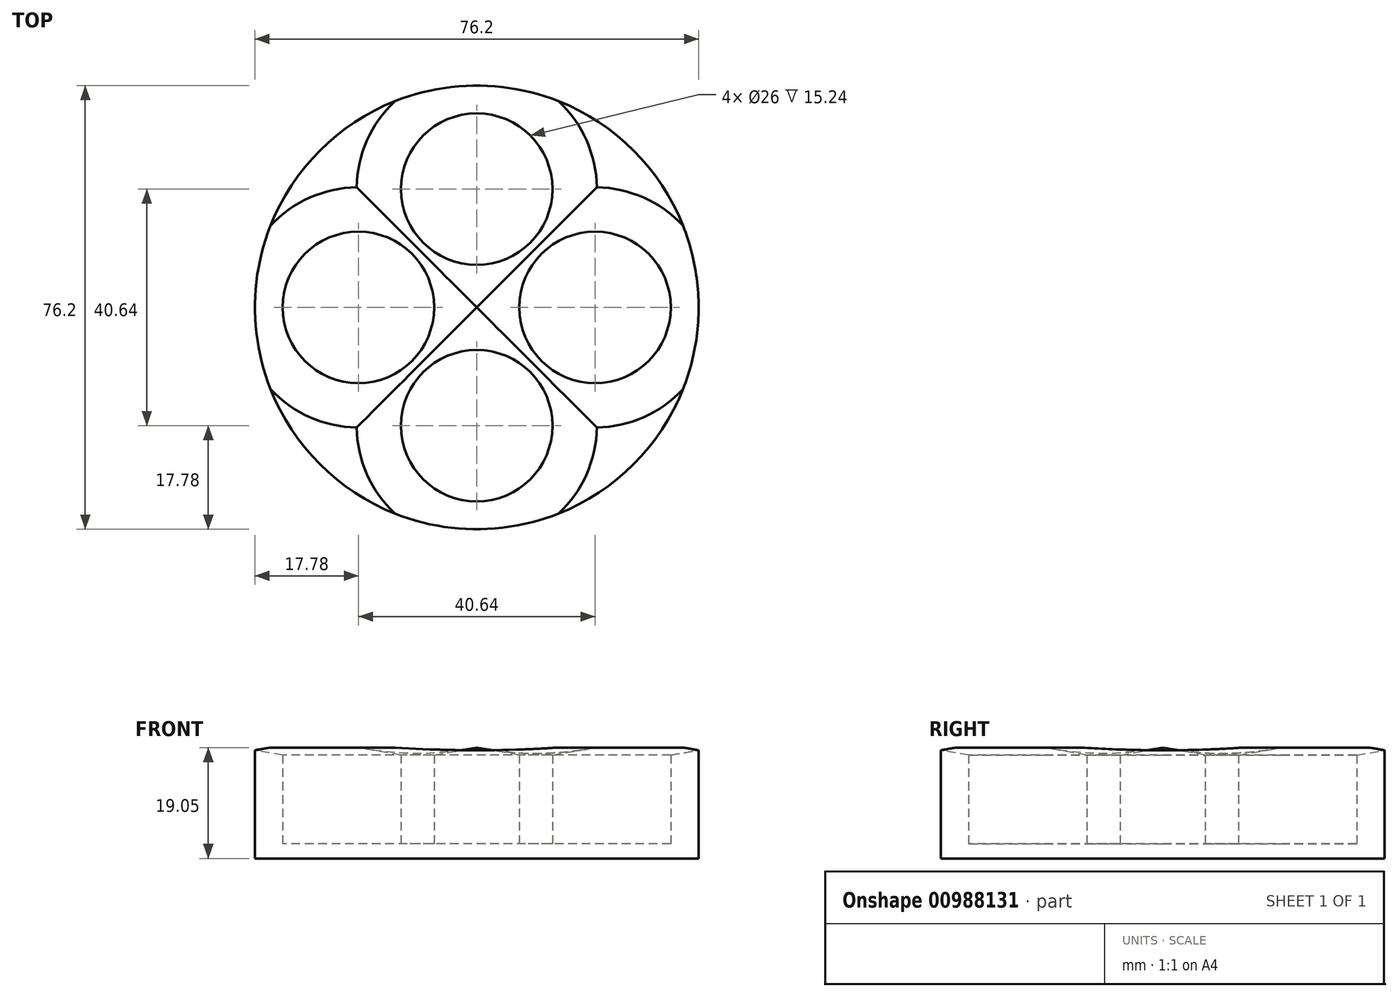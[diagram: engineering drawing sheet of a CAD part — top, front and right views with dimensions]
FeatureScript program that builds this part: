
annotation { "Feature Type Name" : "Feature", "Feature Type Description" : "" }
export const myFeature = defineFeature(function(context is Context, id is Id, definition is map)
    precondition{}
    {
        {
            var Q0;
            Q0=qCreatedBy(makeId("Top.planeOp"),FACE);
            var sketch = newSketch(context, id + "F0", { "sketchPlane" : qUnion([Q0])});
            skCircle(sketch, "E0", {"center": v(0, 0) * mm, "radius": 38.1 * mm});
            skCircle(sketch, "E1", {"center": v(0, 20.32) * mm, "radius": 13 * mm});
            skLineSegment(sketch, "E2", {"start": v(0, 20.32) * mm, "end": v(0, 0) * mm, "construction": true});
            skCircle(sketch, "E3", {"center": v(21.55, 21.55) * mm, "radius": 3.18 * mm});
            skLineSegment(sketch, "E4", {"start": v(0, 0) * mm, "end": v(21.55, 21.55) * mm, "construction": true});
            skCircle(sketch, "E5", {"center": v(21.55, 21.55) * mm, "radius": 5.55 * mm, "construction": true});
            skCircle(sketch, "E6.1.0", {"center": v(-20.32, 0) * mm, "radius": 13 * mm});
            skCircle(sketch, "E6.1.1", {"center": v(-21.55, 21.55) * mm, "radius": 3.18 * mm});
            skCircle(sketch, "E6.2.0", {"center": v(0, -20.32) * mm, "radius": 13 * mm});
            skCircle(sketch, "E6.2.1", {"center": v(-21.55, -21.55) * mm, "radius": 3.18 * mm});
            skCircle(sketch, "E6.3.0", {"center": v(20.32, 0) * mm, "radius": 13 * mm});
            skCircle(sketch, "E6.3.1", {"center": v(21.55, -21.55) * mm, "radius": 3.18 * mm});
            skSolve(sketch);
        }
        {
            var Q0;
            Q0=makeQuery(id+"F0.imprint","IMPRINT",FACE,{"disambiguationData":[TD([[makeQuery(id+"F0.imprint","IMPRINT",EDGE,{"derivedFrom":sQuery(id+"F0.wireOp",EDGE,"E0")}),1.0]])]});
            var Q1;
            Q1=makeQuery(id+"F0.imprint","IMPRINT",FACE,{"disambiguationData":[TD([[makeQuery(id+"F0.imprint","IMPRINT",EDGE,{"derivedFrom":sQuery(id+"F0.wireOp",EDGE,"E6.1.1")}),1.0]])]});
            var Q2;
            Q2=makeQuery(id+"F0.imprint","IMPRINT",FACE,{"disambiguationData":[TD([[makeQuery(id+"F0.imprint","IMPRINT",EDGE,{"derivedFrom":sQuery(id+"F0.wireOp",EDGE,"E6.2.1")}),1.0]])]});
            var Q3;
            Q3=makeQuery(id+"F0.imprint","IMPRINT",FACE,{"disambiguationData":[TD([[makeQuery(id+"F0.imprint","IMPRINT",EDGE,{"derivedFrom":sQuery(id+"F0.wireOp",EDGE,"E6.3.1")}),1.0]])]});
            var Q4;
            Q4=makeQuery(id+"F0.imprint","IMPRINT",FACE,{"disambiguationData":[TD([[makeQuery(id+"F0.imprint","IMPRINT",EDGE,{"derivedFrom":sQuery(id+"F0.wireOp",EDGE,"E3")}),1.0]])]});
            extrude(context, id + "F1", {"entities" : qUnion([Q0, Q1, Q2, Q3, Q4]), "depth" : 19.05 * mm, "offsetDistance" : 25.4 * mm});
        }
        {
            var Q0;
            Q0=makeQuery(id+"F0.imprint","IMPRINT",FACE,{"disambiguationData":[TD([[makeQuery(id+"F0.imprint","IMPRINT",EDGE,{"derivedFrom":sQuery(id+"F0.wireOp",EDGE,"E0")}),1.0]])]});
            var Q1;
            Q1=makeQuery(id+"F0.imprint","IMPRINT",FACE,{"disambiguationData":[TD([[makeQuery(id+"F0.imprint","IMPRINT",EDGE,{"derivedFrom":sQuery(id+"F0.wireOp",EDGE,"E6.1.0")}),1.0]])]});
            var Q2;
            Q2=makeQuery(id+"F0.imprint","IMPRINT",FACE,{"disambiguationData":[TD([[makeQuery(id+"F0.imprint","IMPRINT",EDGE,{"derivedFrom":sQuery(id+"F0.wireOp",EDGE,"E6.2.0")}),1.0]])]});
            var Q3;
            Q3=makeQuery(id+"F0.imprint","IMPRINT",FACE,{"disambiguationData":[TD([[makeQuery(id+"F0.imprint","IMPRINT",EDGE,{"derivedFrom":sQuery(id+"F0.wireOp",EDGE,"E6.3.0")}),1.0]])]});
            var Q4;
            Q4=makeQuery(id+"F0.imprint","IMPRINT",FACE,{"disambiguationData":[TD([[makeQuery(id+"F0.imprint","IMPRINT",EDGE,{"derivedFrom":sQuery(id+"F0.wireOp",EDGE,"E1")}),1.0]])]});
            extrude(context, id + "F2", {"entities" : qUnion([Q0, Q1, Q2, Q3, Q4]), "operationType" : NewBodyOperationType.ADD, "depth" : 2.54 * mm, "offsetDistance" : 25.4 * mm});
        }
        {
            var Q0;
            Q0=makeQuery(id+"F1.opExtrude","CAP_EDGE",EDGE,{"disambiguationData":[OSD([sQuery(id+"F0.wireOp",EDGE,"E6.2.0")])],"isStart":false});
            var Q1;
            Q1=makeQuery(id+"F1.opExtrude","CAP_EDGE",EDGE,{"disambiguationData":[OSD([sQuery(id+"F0.wireOp",EDGE,"E6.1.0")])],"isStart":false});
            var Q2;
            Q2=makeQuery(id+"F1.opExtrude","CAP_EDGE",EDGE,{"disambiguationData":[OSD([sQuery(id+"F0.wireOp",EDGE,"E1")])],"isStart":false});
            var Q3;
            Q3=makeQuery(id+"F1.opExtrude","CAP_EDGE",EDGE,{"disambiguationData":[OSD([sQuery(id+"F0.wireOp",EDGE,"E6.3.0")])],"isStart":false});
            chamfer(context, id + "F3", {"entities" : qUnion([Q0, Q1, Q2, Q3]), "chamferType" : ChamferType.TWO_OFFSETS, "width1" : 7.62 * mm, "oppositeDirection" : false, "width2" : 1.27 * mm, "tangentPropagation" : true});
        }
    });
